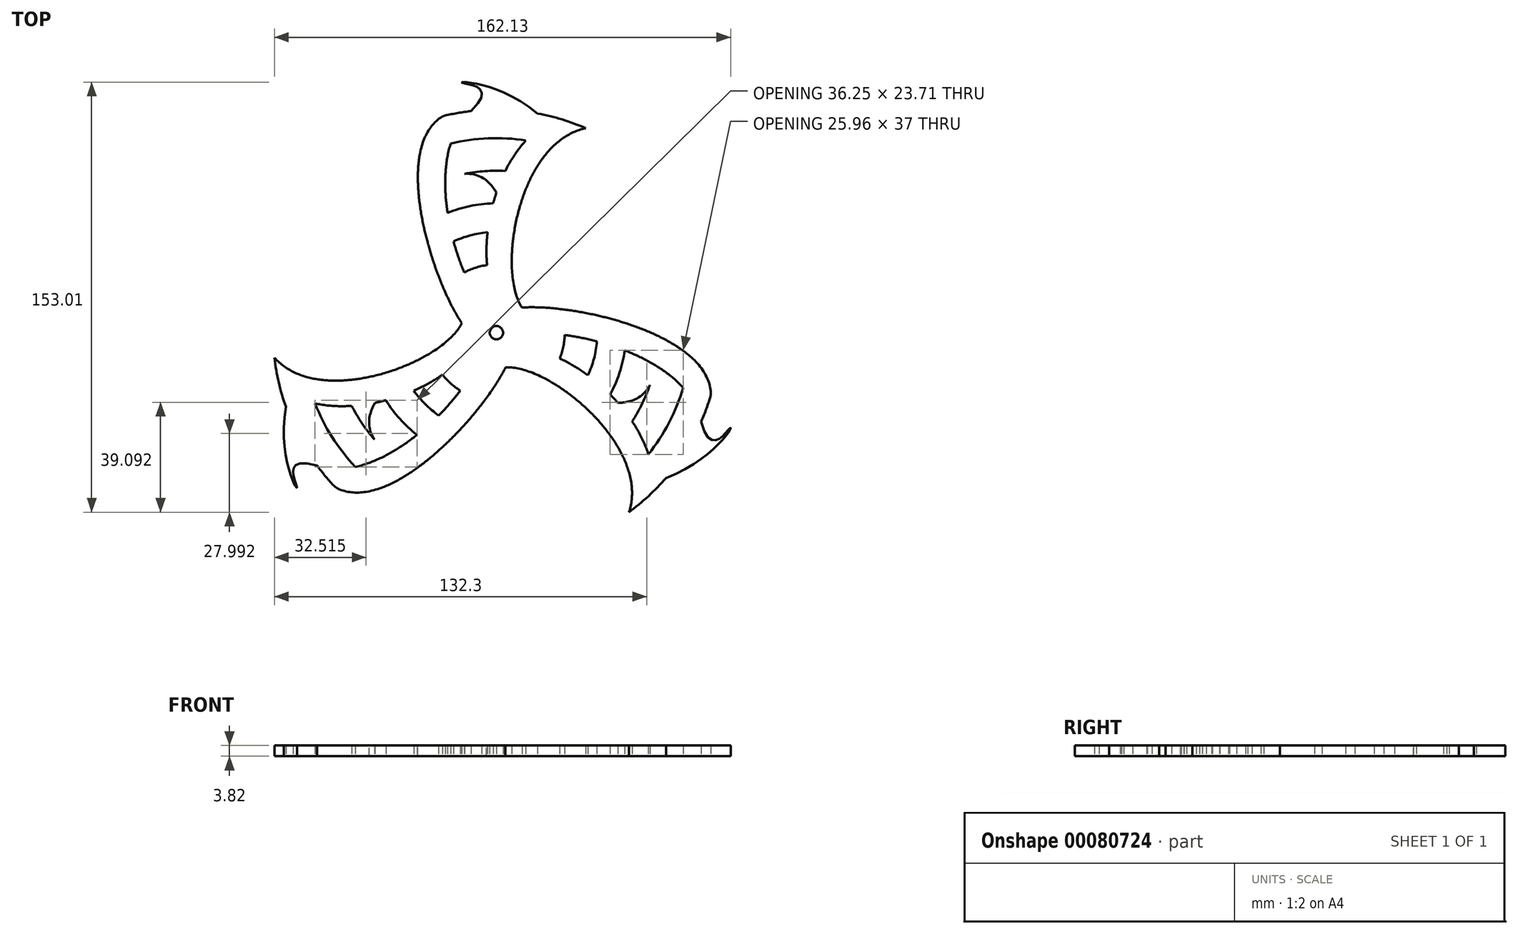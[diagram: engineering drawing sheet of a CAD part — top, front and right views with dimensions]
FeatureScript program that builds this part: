
annotation { "Feature Type Name" : "Feature", "Feature Type Description" : "" }
export const myFeature = defineFeature(function(context is Context, id is Id, definition is map)
    precondition{}
    {
        {
            var Q0;
            Q0=qCreatedBy(makeId("Top.planeOp"),FACE);
            var sketch = newSketch(context, id + "F0", { "sketchPlane" : qUnion([Q0])});
            skCircle(sketch, "E0", {"center": v(0, 0) * mm, "radius": 79.38 * mm});
            skCircle(sketch, "E1", {"center": v(0, 0) * mm, "radius": 2.37 * mm});
            skCircle(sketch, "E2", {"center": v(0, 0) * mm, "radius": 12.7 * mm});
            skFitSpline(sketch, "E3", {"points": [v(-12.26, 3.31) * mm, v(-19.02, 77.06) * mm], "startDerivative": vector(-34.7, 51.98) * mm, "endDerivative": vector(54.42, 32.42) * mm});
            skFitSpline(sketch, "E4", {"points": [v(9.31, 8.64) * mm, v(31.74, 72.75) * mm], "startDerivative": vector(-27.94, 38.71) * mm, "endDerivative": vector(72.54, 15) * mm});
            skFitSpline(sketch, "E5", {"points": [v(14.6, 78.02) * mm, v(-11.69, 88.76) * mm, v(-9.02, 78.86) * mm], "startDerivative": vector(-70.13, 58) * mm, "endDerivative": vector(-72.1, -69.83) * mm});
            skCircle(sketch, "E6", {"center": v(0, 0) * mm, "radius": 69.22 * mm});
            skFitSpline(sketch, "E7", {"points": [v(-5.9, 11.24) * mm, v(-9.02, 78.86) * mm], "startDerivative": vector(-30.89, 42.81) * mm, "endDerivative": vector(50.77, 44.08) * mm});
            skFitSpline(sketch, "E8", {"points": [v(0, 12.7) * mm, v(22.19, 76.21) * mm], "startDerivative": vector(-27.67, 47.04) * mm, "endDerivative": vector(66.57, 20.99) * mm});
            skCircle(sketch, "E9", {"center": v(0, 0) * mm, "radius": 46.04 * mm});
            skCircle(sketch, "E10", {"center": v(0, 0) * mm, "radius": 35.88 * mm});
            skLineSegment(sketch, "E11", {"start": v(-69.21, 0) * mm, "end": v(-46.04, 0) * mm, "construction": true});
            skLineSegment(sketch, "E12", {"start": v(-35.88, 0) * mm, "end": v(-12.7, 0) * mm, "construction": true});
            skLineSegment(sketch, "E13", {"start": v(35.88, 0) * mm, "end": v(46.04, 0) * mm, "construction": true});
            skLineSegment(sketch, "E14", {"start": v(69.21, 0) * mm, "end": v(79.38, 0) * mm, "construction": true});
            skCircle(sketch, "E15", {"center": v(0, 0) * mm, "radius": 57.63 * mm});
            skLineSegment(sketch, "E16", {"start": v(46.04, 0) * mm, "end": v(57.63, 0) * mm, "construction": true});
            skLineSegment(sketch, "E17", {"start": v(57.63, 0) * mm, "end": v(69.21, 0) * mm, "construction": true});
            skFitSpline(sketch, "E18", {"points": [v(0, 49.86) * mm, v(-11.25, 56.52) * mm], "startDerivative": vector(-3.5, 5.56) * mm, "endDerivative": vector(-20.7, -1.7) * mm});
            skCircle(sketch, "E19", {"center": v(0, 0) * mm, "radius": 24.29 * mm});
            skLineSegment(sketch, "E20", {"start": v(12.7, 0) * mm, "end": v(24.29, 0) * mm, "construction": true});
            skLineSegment(sketch, "E21", {"start": v(24.29, 0) * mm, "end": v(35.88, 0) * mm, "construction": true});
            skFitSpline(sketch, "E22", {"points": [v(-2.38, 18.7) * mm, v(-14.97, 19.13) * mm], "startDerivative": vector(-5.42, 2.86) * mm, "endDerivative": vector(-17.92, -7.29) * mm});
            skSolve(sketch);
        }
        {
            var Q0;
            {var subQ0=sQuery(id+"F0.wireOp",EDGE,"E3");Q0=makeQuery(id+"F0.imprint","IMPRINT",FACE,{"disambiguationData":[TD([[makeQuery(id+"F0.imprint","IMPRINT",EDGE,{"derivedFrom":subQ0}),-1.0]])]});}
            var Q1;
            Q1=makeQuery(id+"F0.imprint","IMPRINT",FACE,{"disambiguationData":[TD([[makeQuery(id+"F0.imprint","IMPRINT",EDGE,{"derivedFrom":sQuery(id+"F0.wireOp",EDGE,"E1")}),-1.0]])]});
            var Q2;
            {var subQ0=sQuery(id+"F0.wireOp",EDGE,"E5");Q2=makeQuery(id+"F0.imprint","IMPRINT",FACE,{"disambiguationData":[TD([[makeQuery(id+"F0.imprint","IMPRINT",EDGE,{"derivedFrom":subQ0}),1.0]])]});}
            var Q3;
            {var subQ1=sQuery(id+"F0.wireOp",EDGE,"E5");var subQ2=sQuery(id+"F0.wireOp",EDGE,"E0");var subQ6=makeQuery(id+"F0.imprint","INTERSECT",VERTEX,{"derivedFrom":[subQ2,subQ1]});Q3=makeQuery(id+"F0.imprint","IMPRINT",FACE,{"disambiguationData":[TD([[makeQuery(id+"F0.imprint","IMPRINT",EDGE,{"disambiguationData":[TD([[subQ6,1.0]])],"derivedFrom":subQ2}),1.0]])]});}
            var Q4;
            {var subQ0=sQuery(id+"F0.wireOp",EDGE,"E4");var subQ1=sQuery(id+"F0.wireOp",EDGE,"E0");var subQ2=makeQuery(id+"F0.imprint","INTERSECT",VERTEX,{"derivedFrom":[subQ1,subQ0]});Q4=makeQuery(id+"F0.imprint","IMPRINT",FACE,{"disambiguationData":[TD([[makeQuery(id+"F0.imprint","IMPRINT",EDGE,{"disambiguationData":[TD([[subQ2,-1.0]])],"derivedFrom":subQ1}),1.0]])]});}
            var Q5;
            {var subQ0=sQuery(id+"F0.wireOp",EDGE,"E9");var subQ1=sQuery(id+"F0.wireOp",EDGE,"E4");var subQ2=makeQuery(id+"F0.imprint","INTERSECT",VERTEX,{"derivedFrom":[subQ1,subQ0]});Q5=makeQuery(id+"F0.imprint","IMPRINT",FACE,{"disambiguationData":[TD([[makeQuery(id+"F0.imprint","IMPRINT",EDGE,{"disambiguationData":[TD([[subQ2,-1.0]])],"derivedFrom":subQ1}),1.0]])]});}
            var Q6;
            {var subQ0=sQuery(id+"F0.wireOp",EDGE,"E10");var subQ1=sQuery(id+"F0.wireOp",EDGE,"E4");var subQ2=makeQuery(id+"F0.imprint","INTERSECT",VERTEX,{"derivedFrom":[subQ1,subQ0]});Q6=makeQuery(id+"F0.imprint","IMPRINT",FACE,{"disambiguationData":[TD([[makeQuery(id+"F0.imprint","IMPRINT",EDGE,{"disambiguationData":[TD([[subQ2,-1.0]])],"derivedFrom":subQ1}),1.0]])]});}
            var Q7;
            {var subQ0=sQuery(id+"F0.wireOp",EDGE,"E8");var subQ1=sQuery(id+"F0.wireOp",EDGE,"E2");var subQ2=makeQuery(id+"F0.imprint","INTERSECT",VERTEX,{"derivedFrom":[subQ1,subQ0]});Q7=makeQuery(id+"F0.imprint","IMPRINT",FACE,{"disambiguationData":[TD([[makeQuery(id+"F0.imprint","IMPRINT",EDGE,{"disambiguationData":[TD([[subQ2,1.0]])],"derivedFrom":subQ1}),-1.0]])]});}
            var Q8;
            {var subQ0=sQuery(id+"F0.wireOp",EDGE,"E10");var subQ1=sQuery(id+"F0.wireOp",EDGE,"E7");var subQ2=makeQuery(id+"F0.imprint","INTERSECT",VERTEX,{"derivedFrom":[subQ1,subQ0]});Q8=makeQuery(id+"F0.imprint","IMPRINT",FACE,{"disambiguationData":[TD([[makeQuery(id+"F0.imprint","IMPRINT",EDGE,{"disambiguationData":[TD([[subQ2,-1.0]])],"derivedFrom":subQ1}),-1.0]])]});}
            var Q9;
            {var subQ0=sQuery(id+"F0.wireOp",EDGE,"E9");var subQ1=sQuery(id+"F0.wireOp",EDGE,"E3");var subQ2=makeQuery(id+"F0.imprint","INTERSECT",VERTEX,{"derivedFrom":[subQ1,subQ0]});Q9=makeQuery(id+"F0.imprint","IMPRINT",FACE,{"disambiguationData":[TD([[makeQuery(id+"F0.imprint","IMPRINT",EDGE,{"disambiguationData":[TD([[subQ2,-1.0]])],"derivedFrom":subQ1}),-1.0]])]});}
            var Q10;
            {var subQ0=sQuery(id+"F0.wireOp",EDGE,"02ee5eb9-fec3-4d49-90e1-4be1db1b977d");Q10=makeQuery(id+"F0.imprint","IMPRINT",FACE,{"disambiguationData":[TD([[makeQuery(id+"F0.imprint","IMPRINT",EDGE,{"derivedFrom":subQ0}),1.0]])]});}
            var Q11;
            {var subQ0=sQuery(id+"F0.wireOp",EDGE,"E15");var subQ1=sQuery(id+"F0.wireOp",EDGE,"E4");var subQ2=makeQuery(id+"F0.imprint","INTERSECT",VERTEX,{"derivedFrom":[subQ1,subQ0]});Q11=makeQuery(id+"F0.imprint","IMPRINT",FACE,{"disambiguationData":[TD([[makeQuery(id+"F0.imprint","IMPRINT",EDGE,{"disambiguationData":[TD([[subQ2,-1.0]])],"derivedFrom":subQ1}),1.0]])]});}
            var Q12;
            {var subQ0=sQuery(id+"F0.wireOp",EDGE,"E18");Q12=makeQuery(id+"F0.imprint","IMPRINT",FACE,{"disambiguationData":[TD([[makeQuery(id+"F0.imprint","IMPRINT",EDGE,{"derivedFrom":subQ0}),-1.0]])]});}
            var Q13;
            {var subQ4=sQuery(id+"F0.wireOp",EDGE,"E2");var subQ6=sQuery(id+"F0.wireOp",EDGE,"E3");var subQ7=makeQuery(id+"F0.imprint","INTERSECT",VERTEX,{"derivedFrom":[subQ4,subQ6]});Q13=makeQuery(id+"F0.imprint","IMPRINT",FACE,{"disambiguationData":[TD([[makeQuery(id+"F0.imprint","IMPRINT",EDGE,{"disambiguationData":[TD([[subQ7,1.0]])],"derivedFrom":subQ4}),-1.0]])]});}
            var Q14;
            {var subQ0=sQuery(id+"F0.wireOp",EDGE,"b8c473f6-a033-4eba-b6a9-50cacf2a13a1");Q14=makeQuery(id+"F0.imprint","IMPRINT",FACE,{"disambiguationData":[TD([[makeQuery(id+"F0.imprint","IMPRINT",EDGE,{"derivedFrom":subQ0}),1.0]])]});}
            var Q15;
            {var subQ0=sQuery(id+"F0.wireOp",EDGE,"E19");var subQ1=sQuery(id+"F0.wireOp",EDGE,"E4");var subQ2=makeQuery(id+"F0.imprint","INTERSECT",VERTEX,{"derivedFrom":[subQ1,subQ0]});Q15=makeQuery(id+"F0.imprint","IMPRINT",FACE,{"disambiguationData":[TD([[makeQuery(id+"F0.imprint","IMPRINT",EDGE,{"disambiguationData":[TD([[subQ2,-1.0]])],"derivedFrom":subQ1}),1.0]])]});}
            var Q16;
            {var subQ0=sQuery(id+"F0.wireOp",EDGE,"E22");Q16=makeQuery(id+"F0.imprint","IMPRINT",FACE,{"disambiguationData":[TD([[makeQuery(id+"F0.imprint","IMPRINT",EDGE,{"derivedFrom":subQ0}),-1.0]])]});}
            var Q17;
            {var subQ1=sQuery(id+"F0.wireOp",EDGE,"E3");var subQ5=sQuery(id+"F0.wireOp",EDGE,"E19");var subQ8=makeQuery(id+"F0.imprint","INTERSECT",VERTEX,{"derivedFrom":[subQ1,subQ5]});Q17=makeQuery(id+"F0.imprint","IMPRINT",FACE,{"disambiguationData":[TD([[makeQuery(id+"F0.imprint","IMPRINT",EDGE,{"disambiguationData":[TD([[subQ8,-1.0]])],"derivedFrom":subQ1}),-1.0]])]});}
            var Q18;
            {var subQ0=sQuery(id+"F0.wireOp",EDGE,"E22");var subQ1=sQuery(id+"F0.wireOp",EDGE,"E7");var subQ2=makeQuery(id+"F0.imprint","INTERSECT",VERTEX,{"derivedFrom":[subQ1,subQ0]});Q18=makeQuery(id+"F0.imprint","IMPRINT",FACE,{"disambiguationData":[TD([[makeQuery(id+"F0.imprint","IMPRINT",EDGE,{"disambiguationData":[TD([[subQ2,-1.0]])],"derivedFrom":subQ1}),-1.0]])]});}
            var Q19;
            {var subQ0=sQuery(id+"F0.wireOp",EDGE,"E7");var subQ1=sQuery(id+"F0.wireOp",EDGE,"E2");var subQ2=makeQuery(id+"F0.imprint","INTERSECT",VERTEX,{"derivedFrom":[subQ1,subQ0]});Q19=makeQuery(id+"F0.imprint","IMPRINT",FACE,{"disambiguationData":[TD([[makeQuery(id+"F0.imprint","IMPRINT",EDGE,{"disambiguationData":[TD([[subQ2,1.0]])],"derivedFrom":subQ1}),-1.0]])]});}
            extrude(context, id + "F1", {"entities" : qUnion([Q0, Q1, Q2, Q3, Q4, Q5, Q6, Q7, Q8, Q9, Q10, Q11, Q12, Q13, Q14, Q15, Q16, Q17, Q18, Q19]), "endBound" : BoundingType.SYMMETRIC, "depth" : 3.8 * mm});
        }
        {
            var Q0;
            Q0=makeQuery(id+"F1.opExtrude","SWEPT_BODY",BODY,{"disambiguationData":[OSD([sQuery(id+"F0.wireOp",EDGE,"E0"),sQuery(id+"F0.wireOp",EDGE,"E1"),sQuery(id+"F0.wireOp",EDGE,"E2"),sQuery(id+"F0.wireOp",EDGE,"E3"),sQuery(id+"F0.wireOp",EDGE,"E4"),sQuery(id+"F0.wireOp",EDGE,"E5")])]});
            var Q1;
            Q1=makeQuery(id+"F1.opExtrude","CAP_EDGE",EDGE,{"disambiguationData":[OSD([sQuery(id+"F0.wireOp",EDGE,"E1")])],"isStart":false});
            circularPattern(context, id + "F2", {"operationType" : NewBodyOperationType.ADD, "entities" : qUnion([Q0]), "axis" : qUnion([Q1]), "angle" : 360 * degree, "instanceCount" : 3, "equalSpace" : true});
        }
        {
            var Q0;
            Q0=makeQuery(id+"F1.opExtrude","SWEPT_EDGE",EDGE,{"disambiguationData":[OSD([sQuery(id+"F0.wireOp",EDGE,"E0"),sQuery(id+"F0.wireOp",EDGE,"E3")])]});
            var Q1;
            Q1=makeQuery(id+"F2.opPattern","COPY",EDGE,{"derivedFrom":makeQuery(id+"F1.opExtrude","SWEPT_EDGE",EDGE,{"disambiguationData":[OSD([sQuery(id+"F0.wireOp",EDGE,"E0"),sQuery(id+"F0.wireOp",EDGE,"E3")])]}),"instanceName":"1"});
            fillet(context, id + "F3", {"entities" : qUnion([Q0, Q1]), "radius" : 5.08 * mm, "tangentPropagation" : true, "allowEdgeOverflow" : false});
        }
    });
